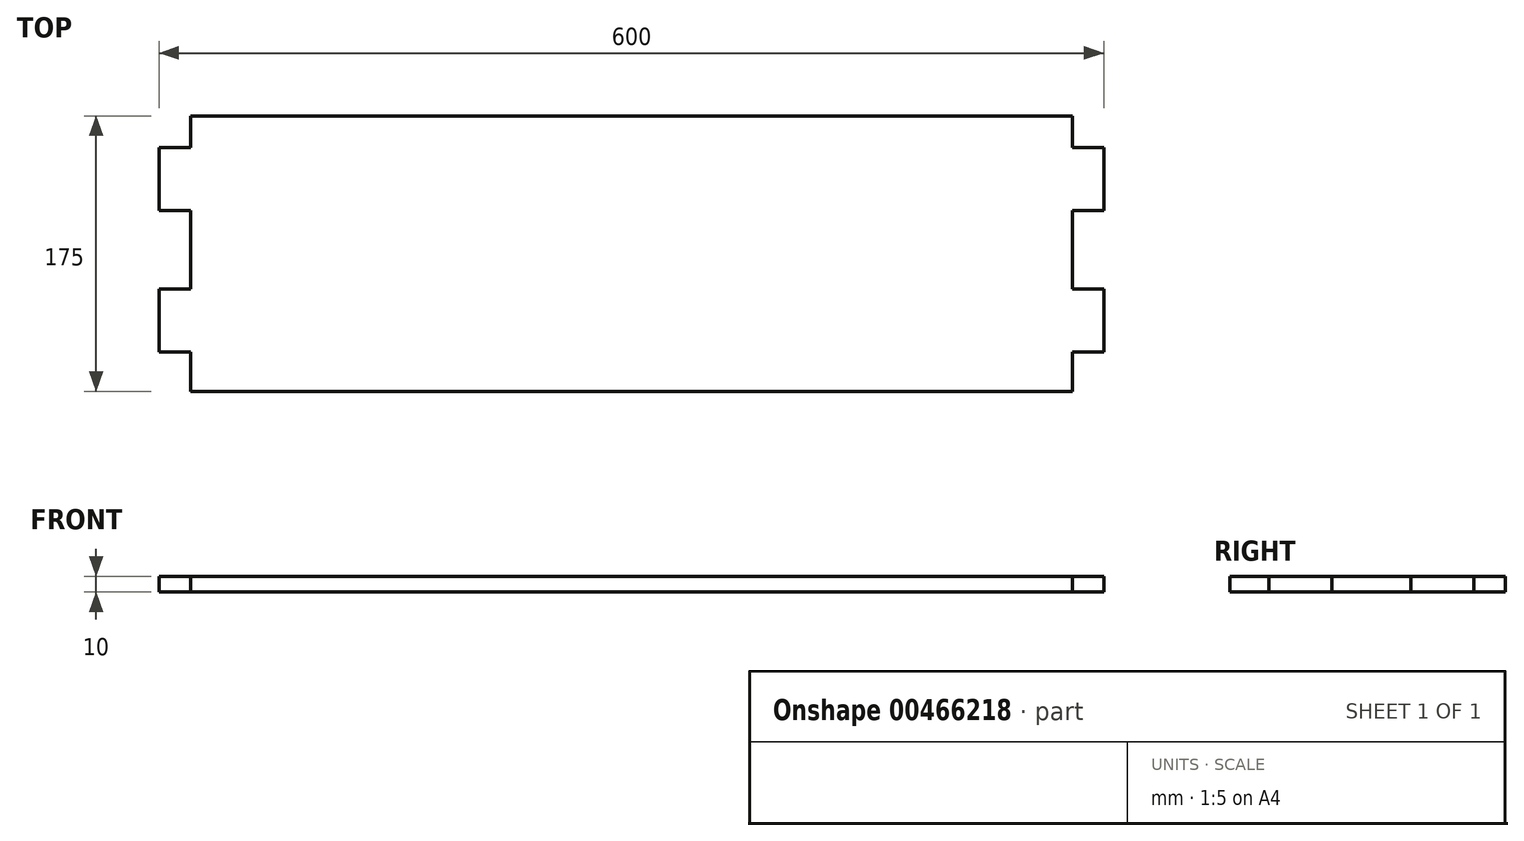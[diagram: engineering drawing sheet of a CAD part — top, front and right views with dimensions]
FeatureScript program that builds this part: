
annotation { "Feature Type Name" : "Feature", "Feature Type Description" : "" }
export const myFeature = defineFeature(function(context is Context, id is Id, definition is map)
    precondition{}
    {
        {
            var Q0;
            Q0=qCreatedBy(makeId("Top.planeOp"),FACE);
            var sketch = newSketch(context, id + "F0", { "sketchPlane" : qUnion([Q0])});
            skLineSegment(sketch, "E0.bottom", {"start": v(-293.72, -23.62) * mm, "end": v(306.28, -23.62) * mm});
            skLineSegment(sketch, "E0.top", {"start": v(-293.72, -198.62) * mm, "end": v(306.28, -198.62) * mm});
            skLineSegment(sketch, "E0.left", {"start": v(-293.72, -23.62) * mm, "end": v(-293.72, -198.62) * mm});
            skLineSegment(sketch, "E0.right", {"start": v(306.28, -23.62) * mm, "end": v(306.28, -198.62) * mm});
            skSolve(sketch);
        }
        {
            var Q0;
            Q0 = qSketchRegion(id + "F0", true);
            extrude(context, id + "F1", {"entities" : qUnion([Q0]), "depth" : 10 * mm, "offsetDistance" : 25 * mm});
        }
        {
            var Q0;
            Q0=makeQuery(id+"F1.opExtrude","CAP_FACE",FACE,{"disambiguationData":[OSD([sQuery(id+"F0.wireOp",EDGE,"E0.bottom"),sQuery(id+"F0.wireOp",EDGE,"E0.top"),sQuery(id+"F0.wireOp",EDGE,"E0.left"),sQuery(id+"F0.wireOp",EDGE,"E0.right")])],"isStart":false});
            var sketch = newSketch(context, id + "F2", { "sketchPlane" : qUnion([Q0])});
            skLineSegment(sketch, "E1.bottom", {"start": v(-293.72, -23.62) * mm, "end": v(-273.72, -23.62) * mm});
            skLineSegment(sketch, "E1.top", {"start": v(-293.72, -43.62) * mm, "end": v(-273.72, -43.62) * mm});
            skLineSegment(sketch, "E1.left", {"start": v(-293.72, -23.62) * mm, "end": v(-293.72, -43.62) * mm});
            skLineSegment(sketch, "E1.right", {"start": v(-273.72, -23.62) * mm, "end": v(-273.72, -43.62) * mm});
            skLineSegment(sketch, "E2.bottom", {"start": v(-293.72, -83.62) * mm, "end": v(-273.72, -83.62) * mm});
            skLineSegment(sketch, "E2.top", {"start": v(-293.72, -133.62) * mm, "end": v(-273.72, -133.62) * mm});
            skLineSegment(sketch, "E2.left", {"start": v(-293.72, -83.62) * mm, "end": v(-293.72, -133.62) * mm});
            skLineSegment(sketch, "E2.right", {"start": v(-273.72, -83.62) * mm, "end": v(-273.72, -133.62) * mm});
            skLineSegment(sketch, "E3.bottom", {"start": v(-293.72, -198.62) * mm, "end": v(-273.72, -198.62) * mm});
            skLineSegment(sketch, "E3.top", {"start": v(-293.72, -173.62) * mm, "end": v(-273.72, -173.62) * mm});
            skLineSegment(sketch, "E3.left", {"start": v(-293.72, -198.62) * mm, "end": v(-293.72, -173.62) * mm});
            skLineSegment(sketch, "E3.right", {"start": v(-273.72, -198.62) * mm, "end": v(-273.72, -173.62) * mm});
            skLineSegment(sketch, "E4.bottom", {"start": v(306.28, -198.62) * mm, "end": v(286.28, -198.62) * mm});
            skLineSegment(sketch, "E4.top", {"start": v(306.28, -173.62) * mm, "end": v(286.28, -173.62) * mm});
            skLineSegment(sketch, "E4.left", {"start": v(306.28, -198.62) * mm, "end": v(306.28, -173.62) * mm});
            skLineSegment(sketch, "E4.right", {"start": v(286.28, -198.62) * mm, "end": v(286.28, -173.62) * mm});
            skLineSegment(sketch, "E5.bottom", {"start": v(306.28, -133.62) * mm, "end": v(286.28, -133.62) * mm});
            skLineSegment(sketch, "E5.top", {"start": v(306.28, -83.62) * mm, "end": v(286.28, -83.62) * mm});
            skLineSegment(sketch, "E5.left", {"start": v(306.28, -133.62) * mm, "end": v(306.28, -83.62) * mm});
            skLineSegment(sketch, "E5.right", {"start": v(286.28, -133.62) * mm, "end": v(286.28, -83.62) * mm});
            skLineSegment(sketch, "E6.bottom", {"start": v(306.28, -23.62) * mm, "end": v(286.28, -23.62) * mm});
            skLineSegment(sketch, "E6.top", {"start": v(306.28, -43.62) * mm, "end": v(286.28, -43.62) * mm});
            skLineSegment(sketch, "E6.left", {"start": v(306.28, -23.62) * mm, "end": v(306.28, -43.62) * mm});
            skLineSegment(sketch, "E6.right", {"start": v(286.28, -23.62) * mm, "end": v(286.28, -43.62) * mm});
            skSolve(sketch);
        }
        {
            var Q0;
            Q0=makeQuery(id+"F2.imprint","IMPRINT",FACE,{"disambiguationData":[TD([[makeQuery(id+"F2.imprint","IMPRINT",EDGE,{"derivedFrom":sQuery(id+"F2.wireOp",EDGE,"E6.bottom")}),-1.0]])]});
            var Q1;
            Q1=makeQuery(id+"F2.imprint","IMPRINT",FACE,{"disambiguationData":[TD([[makeQuery(id+"F2.imprint","IMPRINT",EDGE,{"derivedFrom":sQuery(id+"F2.wireOp",EDGE,"E5.bottom")}),-1.0]])]});
            var Q2;
            Q2=makeQuery(id+"F2.imprint","IMPRINT",FACE,{"disambiguationData":[TD([[makeQuery(id+"F2.imprint","IMPRINT",EDGE,{"derivedFrom":sQuery(id+"F2.wireOp",EDGE,"E4.bottom")}),1.0]])]});
            var Q3;
            Q3=makeQuery(id+"F2.imprint","IMPRINT",FACE,{"disambiguationData":[TD([[makeQuery(id+"F2.imprint","IMPRINT",EDGE,{"derivedFrom":sQuery(id+"F2.wireOp",EDGE,"E3.bottom")}),1.0]])]});
            var Q4;
            Q4=makeQuery(id+"F2.imprint","IMPRINT",FACE,{"disambiguationData":[TD([[makeQuery(id+"F2.imprint","IMPRINT",EDGE,{"derivedFrom":sQuery(id+"F2.wireOp",EDGE,"E2.bottom")}),-1.0]])]});
            var Q5;
            Q5=makeQuery(id+"F2.imprint","IMPRINT",FACE,{"disambiguationData":[TD([[makeQuery(id+"F2.imprint","IMPRINT",EDGE,{"derivedFrom":sQuery(id+"F2.wireOp",EDGE,"E1.bottom")}),-1.0]])]});
            extrude(context, id + "F3", {"entities" : qUnion([Q0, Q1, Q2, Q3, Q4, Q5]), "operationType" : NewBodyOperationType.REMOVE, "endBound" : BoundingType.THROUGH_ALL, "oppositeDirection" : true, "depth" : 25 * mm, "offsetDistance" : 25 * mm});
        }
    });
